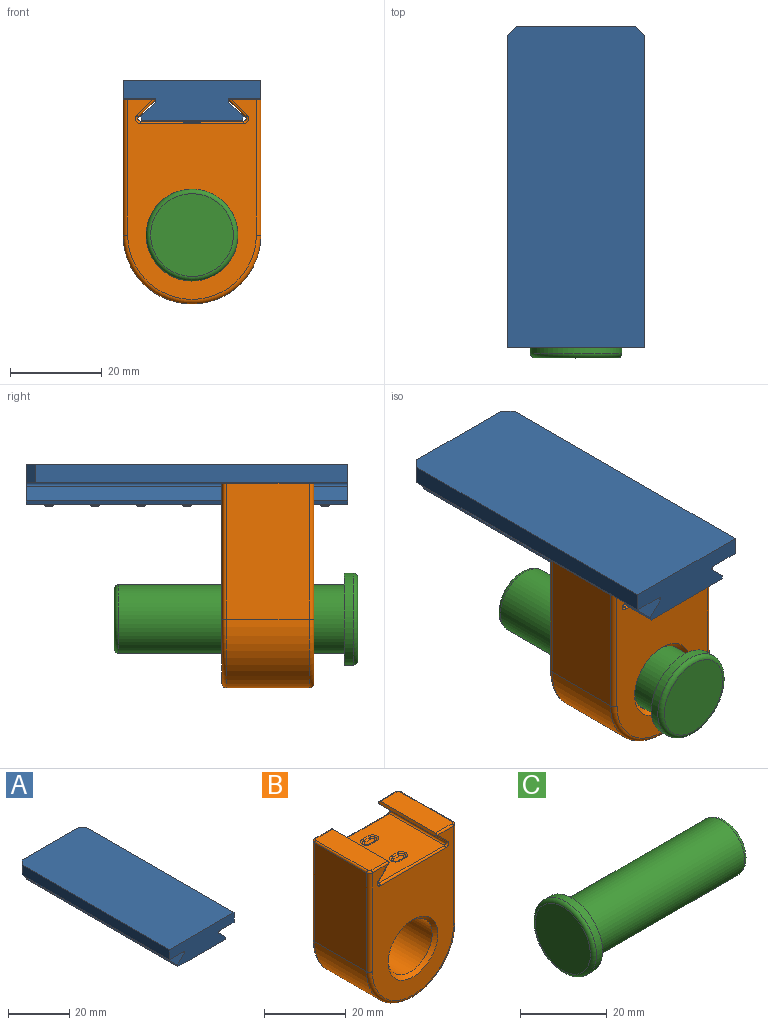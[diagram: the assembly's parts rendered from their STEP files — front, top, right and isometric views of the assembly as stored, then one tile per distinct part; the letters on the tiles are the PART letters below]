
ASSEMBLY  parts=3 mates=3
PART A: 79 faces, bbox 30x70x9.3 mm
  f0: cylinder r=0.5mm len=2mm, axis (-1,0,0), area 1mm2, adj f1,f2,f4,f59
  f1: torus R=1.37mm, axis (0,0,-1), area 1.9mm2, adj f0,f3,f5,f59
  f2: torus R=1.37mm, axis (0,0,-1), area 1.9mm2, adj f0,f3,f6,f59
  f3: cylinder r=0.5mm len=2mm, axis (1,0,0), area 1mm2, adj f1,f2,f7,f59
  f4: cylinder r=0.5mm len=2mm, axis (-1,0,0), area 1mm2, adj f0,f5,f6,f8
  f5: torus R=0.5mm, axis (0,0,-1), area 1.2mm2, adj f1,f4,f7,f8
  f6: torus R=0.5mm, axis (0,0,-1), area 1.2mm2, adj f2,f4,f7,f8
  f7: cylinder r=0.5mm len=2mm, axis (1,0,0), area 1mm2, adj f3,f5,f6,f8
  f8: plane 3x1mm, normal (0,0,-1), area 2.8mm2, adj f4,f5,f6,f7
  f9: cylinder r=0.5mm len=2mm, axis (-1,0,0), area 1mm2, adj f10,f11,f13,f59
  f10: torus R=1.37mm, axis (0,0,-1), area 1.9mm2, adj f9,f12,f14,f59
  f11: torus R=1.37mm, axis (0,0,-1), area 1.9mm2, adj f9,f12,f15,f59
  f12: cylinder r=0.5mm len=2mm, axis (1,0,0), area 1mm2, adj f10,f11,f16,f59
  f13: cylinder r=0.5mm len=2mm, axis (-1,0,0), area 1mm2, adj f9,f14,f15,f17
  f14: torus R=0.5mm, axis (0,0,-1), area 1.2mm2, adj f10,f13,f16,f17
  f15: torus R=0.5mm, axis (0,0,-1), area 1.2mm2, adj f11,f13,f16,f17
  f16: cylinder r=0.5mm len=2mm, axis (1,0,0), area 1mm2, adj f12,f14,f15,f17
  f17: plane 3x1mm, normal (0,0,-1), area 2.8mm2, adj f13,f14,f15,f16
  f18: cylinder r=0.5mm len=2mm, axis (-1,0,0), area 1mm2, adj f19,f20,f22,f59
  f19: torus R=1.37mm, axis (0,0,-1), area 1.9mm2, adj f18,f21,f23,f59
  f20: torus R=1.37mm, axis (0,0,-1), area 1.9mm2, adj f18,f21,f24,f59
  f21: cylinder r=0.5mm len=2mm, axis (1,0,0), area 1mm2, adj f19,f20,f25,f59
  f22: cylinder r=0.5mm len=2mm, axis (-1,0,0), area 1mm2, adj f18,f23,f24,f26
  f23: torus R=0.5mm, axis (0,0,-1), area 1.2mm2, adj f19,f22,f25,f26
  f24: torus R=0.5mm, axis (0,0,-1), area 1.2mm2, adj f20,f22,f25,f26
  f25: cylinder r=0.5mm len=2mm, axis (1,0,0), area 1mm2, adj f21,f23,f24,f26
  f26: plane 3x1mm, normal (0,0,-1), area 2.8mm2, adj f22,f23,f24,f25
  f27: cylinder r=0.5mm len=2mm, axis (-1,0,0), area 1mm2, adj f28,f29,f31,f59
  f28: torus R=1.37mm, axis (0,0,-1), area 1.9mm2, adj f27,f30,f32,f59
  f29: torus R=1.37mm, axis (0,0,-1), area 1.9mm2, adj f27,f30,f33,f59
  f30: cylinder r=0.5mm len=2mm, axis (1,0,0), area 1mm2, adj f28,f29,f34,f59
  f31: cylinder r=0.5mm len=2mm, axis (-1,0,0), area 1mm2, adj f27,f32,f33,f35
  f32: torus R=0.5mm, axis (0,0,-1), area 1.2mm2, adj f28,f31,f34,f35
  f33: torus R=0.5mm, axis (0,0,-1), area 1.2mm2, adj f29,f31,f34,f35
  f34: cylinder r=0.5mm len=2mm, axis (1,0,0), area 1mm2, adj f30,f32,f33,f35
  f35: plane 3x1mm, normal (0,0,-1), area 2.8mm2, adj f31,f32,f33,f34
  f36: cylinder r=0.5mm len=2mm, axis (-1,0,0), area 1mm2, adj f37,f38,f40,f59
  f37: torus R=1.37mm, axis (0,0,-1), area 1.9mm2, adj f36,f39,f41,f59
  f38: torus R=1.37mm, axis (0,0,-1), area 1.9mm2, adj f36,f39,f42,f59
  f39: cylinder r=0.5mm len=2mm, axis (1,0,0), area 1mm2, adj f37,f38,f43,f59
  f40: cylinder r=0.5mm len=2mm, axis (-1,0,0), area 1mm2, adj f36,f41,f42,f44
  f41: torus R=0.5mm, axis (0,0,-1), area 1.2mm2, adj f37,f40,f43,f44
  f42: torus R=0.5mm, axis (0,0,-1), area 1.2mm2, adj f38,f40,f43,f44
  f43: cylinder r=0.5mm len=2mm, axis (1,0,0), area 1mm2, adj f39,f41,f42,f44
  f44: plane 3x1mm, normal (0,0,-1), area 2.8mm2, adj f40,f41,f42,f43
  f45: cylinder r=0.5mm len=2mm, axis (-1,0,0), area 1mm2, adj f46,f47,f49,f59
  f46: torus R=1.37mm, axis (0,0,-1), area 1.9mm2, adj f45,f48,f50,f59
  f47: torus R=1.37mm, axis (0,0,-1), area 1.9mm2, adj f45,f48,f51,f59
  f48: cylinder r=0.5mm len=2mm, axis (1,0,0), area 1mm2, adj f46,f47,f52,f59
  f49: cylinder r=0.5mm len=2mm, axis (-1,0,0), area 1mm2, adj f45,f50,f51,f53
  f50: torus R=0.5mm, axis (0,0,-1), area 1.2mm2, adj f46,f49,f52,f53
  f51: torus R=0.5mm, axis (0,0,-1), area 1.2mm2, adj f47,f49,f52,f53
  f52: cylinder r=0.5mm len=2mm, axis (1,0,0), area 1mm2, adj f48,f50,f51,f53
  f53: plane 3x1mm, normal (0,0,-1), area 2.8mm2, adj f49,f50,f51,f52
  f54: plane 68x4mm, normal (1,0,0), area 272mm2, adj f55,f61,f62,f69
  f55: plane 70x30mm, normal (0,0,1), area 2096mm2, adj f54,f56,f62,f63,f68,f69
  f56: plane 68x4mm, normal (-1,0,0), area 272mm2, adj f55,f57,f62,f68
  f57: plane 70x6.65mm, normal (0,0,-1), area 463.3mm2, adj f56,f62,f63,f66,f68
  f58: plane 70x3.19mm, normal (-0.71,0,0.71), area 315.7mm2, adj f62,f63,f65,f66
  f59: plane 70x21.79mm, normal (0,0,-1), area 1446.2mm2, adj f0,f1,f2,f3,f9,f10,f11,f12
  f60: plane 70x3.19mm, normal (0.71,0,0.71), area 315.7mm2, adj f62,f63,f64,f67
  f61: plane 70x6.65mm, normal (0,0,-1), area 463.3mm2, adj f54,f62,f63,f67,f69
  f62: plane 30x8.75mm, normal (0,-1,0), area 210.4mm2, adj f54,f55,f56,f57,f58,f59,f60,f61
  f63: plane 26x8.75mm, normal (0,1,0), area 194.4mm2, adj f55,f57,f58,f59,f60,f61,f64,f65
  f64: plane 70x0.71mm, normal (0.92,0,-0.38), area 53.6mm2, adj f59,f60,f62,f63
  f65: plane 70x0.71mm, normal (-0.92,0,-0.38), area 53.6mm2, adj f58,f59,f62,f63
  f66: cylinder r=0.5mm len=70mm, axis (0,-1,0), area 82.5mm2, adj f57,f58,f62,f63
  f67: cylinder r=0.5mm len=70mm, axis (0,-1,0), area 82.5mm2, adj f60,f61,f62,f63
  f68: plane 4x2mm, normal (-0.71,0.71,0), area 11.3mm2, adj f55,f56,f57,f63
  f69: plane 4x2mm, normal (0.71,0.71,0), area 11.3mm2, adj f54,f55,f61,f63
  f70: plane 3x1mm, normal (0,0,-1), area 2.8mm2, adj f71,f72,f73,f74
  f71: cylinder r=0.5mm len=2mm, axis (-1,0,0), area 1mm2, adj f70,f72,f73,f75
  f72: torus R=0.5mm, axis (0,0,-1), area 1.2mm2, adj f70,f71,f74,f76
  f73: torus R=0.5mm, axis (0,0,-1), area 1.2mm2, adj f70,f71,f74,f77
  f74: cylinder r=0.5mm len=2mm, axis (1,0,0), area 1mm2, adj f70,f72,f73,f78
  f75: cylinder r=0.5mm len=2mm, axis (-1,0,0), area 1mm2, adj f59,f71,f76,f77
  f76: torus R=1.37mm, axis (0,0,-1), area 1.9mm2, adj f59,f72,f75,f78
  f77: torus R=1.37mm, axis (0,0,-1), area 1.9mm2, adj f59,f73,f75,f78
  f78: cylinder r=0.5mm len=2mm, axis (1,0,0), area 1mm2, adj f59,f74,f76,f77
PART B: 61 faces, bbox 32.5x20.2x46.2 mm
  f0: cylinder r=0.5mm len=2mm, axis (1,0,0), area 1mm2, adj f1,f2,f4,f8
  f1: torus R=0.63mm, axis (0,0,-1), area 1.4mm2, adj f0,f3,f5,f8
  f2: torus R=0.63mm, axis (0,0,-1), area 1.4mm2, adj f0,f3,f6,f8
  f3: cylinder r=0.5mm len=2mm, axis (-1,0,0), area 1mm2, adj f1,f2,f7,f8
  f4: cylinder r=0.5mm len=2mm, axis (1,0,0), area 1mm2, adj f0,f5,f6,f9
  f5: torus R=1.5mm, axis (0,0,1), area 2.1mm2, adj f1,f4,f7,f9
  f6: torus R=1.5mm, axis (0,0,1), area 2.1mm2, adj f2,f4,f7,f9
  f7: cylinder r=0.5mm len=2mm, axis (-1,0,0), area 1mm2, adj f3,f5,f6,f9
  f8: plane 3.27x1.27mm, normal (0,0,1), area 3.8mm2, adj f0,f1,f2,f3
  f9: plane 22.59x19mm, normal (0,0,1), area 403mm2, adj f4,f5,f6,f7,f22,f23,f25,f26
  f10: plane 29.5x18mm, normal (-1,0,0), area 531mm2, adj f11,f37,f40,f43
  f11: cylinder r=15mm len=30mm, axis (0,1,0), area 848.2mm2, adj f10,f12,f36,f39
  f12: plane 29.5x18mm, normal (1,0,0), area 531mm2, adj f11,f35,f38,f48
  f13: plane 19x6.2mm, normal (0,0,1), area 117.7mm2, adj f20,f46,f47,f48,f49,f50
  f14: plane 19x3.64mm, normal (-0.71,0,-0.71), area 97.8mm2, adj f20,f22,f51,f56
  f15: plane 19x3.64mm, normal (0.71,0,-0.71), area 97.8mm2, adj f21,f23,f55,f60
  f16: cylinder r=7.6mm len=18mm, axis (0,1,0), area 859.5mm2, adj f33,f34
  f17: plane 19x6.2mm, normal (0,0,1), area 117.7mm2, adj f21,f41,f42,f43,f44,f45
  f18: plane 43.5x28mm, normal (0,-1,0), area 788.5mm2, adj f34,f38,f39,f40,f41,f46,f51,f52
  f19: plane 43.5x28mm, normal (0,1,0), area 788.5mm2, adj f33,f35,f36,f37,f45,f50,f56,f57
  f20: plane 19.96x0.71mm, normal (-0.92,0,0.38), area 15.1mm2, adj f13,f14,f46,f50,f51,f56
  f21: plane 19.96x0.71mm, normal (0.92,0,0.38), area 15.1mm2, adj f15,f17,f41,f45,f55,f60
  f22: cylinder r=0.5mm len=19mm, axis (0,-1,0), area 22.4mm2, adj f9,f14,f52,f57
  f23: cylinder r=0.5mm len=19mm, axis (0,-1,0), area 22.4mm2, adj f9,f15,f54,f59
  f24: plane 3.27x1.27mm, normal (0,0,1), area 3.8mm2, adj f29,f30,f31,f32
  f25: cylinder r=0.5mm len=2mm, axis (1,0,0), area 1mm2, adj f9,f26,f27,f29
  f26: torus R=1.5mm, axis (0,0,1), area 2.1mm2, adj f9,f25,f28,f30
  f27: torus R=1.5mm, axis (0,0,1), area 2.1mm2, adj f9,f25,f28,f31
  f28: cylinder r=0.5mm len=2mm, axis (-1,0,0), area 1mm2, adj f9,f26,f27,f32
  f29: cylinder r=0.5mm len=2mm, axis (1,0,0), area 1mm2, adj f24,f25,f30,f31
  f30: torus R=0.63mm, axis (0,0,-1), area 1.4mm2, adj f24,f26,f29,f32
  f31: torus R=0.63mm, axis (0,0,-1), area 1.4mm2, adj f24,f27,f29,f32
  f32: cylinder r=0.5mm len=2mm, axis (-1,0,0), area 1mm2, adj f24,f28,f30,f31
  f33: cone r=8.6mm half-angle=45deg, axis (0,1,0), area 72mm2, adj f16,f19
  f34: cone r=7.6mm half-angle=45deg, axis (0,-1,0), area 72mm2, adj f16,f18
  f35: cylinder r=1mm len=29.5mm, axis (0,0,1), area 46.3mm2, adj f12,f19,f36,f49
  f36: torus R=14mm, axis (0,-1,0), area 72.2mm2, adj f11,f19,f35,f37
  f37: cylinder r=1mm len=29.5mm, axis (0,0,-1), area 46.3mm2, adj f10,f19,f36,f44
  f38: cylinder r=1mm len=29.5mm, axis (0,0,-1), area 46.3mm2, adj f12,f18,f39,f47
  f39: torus R=14mm, axis (0,-1,0), area 72.2mm2, adj f11,f18,f38,f40
  f40: cylinder r=1mm len=29.5mm, axis (0,0,1), area 46.3mm2, adj f10,f18,f39,f42
  f41: cylinder r=0.5mm len=5.85mm, axis (1,0,0), area 4.5mm2, adj f17,f18,f21,f42,f55
  f42: torus R=0.5mm, axis (0,0,1), area 1mm2, adj f17,f40,f41,f43
  f43: cylinder r=0.5mm len=18mm, axis (0,1,0), area 14.1mm2, adj f10,f17,f42,f44
  f44: torus R=0.5mm, axis (0,0,1), area 1mm2, adj f17,f37,f43,f45
  f45: cylinder r=0.5mm len=5.85mm, axis (-1,0,0), area 4.5mm2, adj f17,f19,f21,f44,f60
  f46: cylinder r=0.5mm len=5.85mm, axis (1,0,0), area 4.5mm2, adj f13,f18,f20,f47,f51
  f47: torus R=0.5mm, axis (0,0,1), area 1mm2, adj f13,f38,f46,f48
  f48: cylinder r=0.5mm len=18mm, axis (0,1,0), area 14.1mm2, adj f12,f13,f47,f49
  f49: torus R=0.5mm, axis (0,0,1), area 1mm2, adj f13,f35,f48,f50
  f50: cylinder r=0.5mm len=5.85mm, axis (-1,0,0), area 4.5mm2, adj f13,f19,f20,f49,f56
  f51: cylinder r=0.5mm len=4.1mm, axis (-0.71,0,0.71), area 4.1mm2, adj f14,f18,f20,f46,f52
  f52: torus R=1mm, axis (0,-1,0), area 1.3mm2, adj f18,f22,f51,f53
  f53: cylinder r=0.5mm len=22.59mm, axis (1,0,0), area 17.7mm2, adj f9,f18,f52,f54
  f54: torus R=1mm, axis (0,-1,0), area 1.3mm2, adj f18,f23,f53,f55
  f55: cylinder r=0.5mm len=4.1mm, axis (-0.71,0,-0.71), area 4.1mm2, adj f15,f18,f21,f41,f54
  f56: cylinder r=0.5mm len=4.1mm, axis (0.71,0,-0.71), area 4.1mm2, adj f14,f19,f20,f50,f57
  f57: torus R=1mm, axis (0,-1,0), area 1.3mm2, adj f19,f22,f56,f58
  f58: cylinder r=0.5mm len=22.59mm, axis (-1,0,0), area 17.7mm2, adj f9,f19,f57,f59
  f59: torus R=1mm, axis (0,-1,0), area 1.3mm2, adj f19,f23,f58,f60
  f60: cylinder r=0.5mm len=4.1mm, axis (0.71,0,0.71), area 4.1mm2, adj f15,f19,f21,f45,f59
PART C: 7 faces, bbox 53x21.6x21.6 mm
  f0: cylinder r=7.45mm len=49mm, axis (-1,0,0), area 2293.7mm2, adj f2,f5
  f1: plane 12.9x12.9mm, normal (1,0,0), area 130.7mm2, adj f2
  f2: torus R=6.45mm, axis (1,0,0), area 69.9mm2, adj f0,f1
  f3: cylinder r=10mm len=20mm, axis (1,0,0), area 125.7mm2, adj f5,f6
  f4: plane 18x18mm, normal (-1,0,0), area 254.5mm2, adj f6
  f5: plane 20x20mm, normal (1,0,0), area 139.8mm2, adj f0,f3
  f6: torus R=9mm, axis (-1,0,0), area 95.1mm2, adj f3,f4
PLACE A t=(-23.82,10.52,-11.33)mm fixed
PLACE B t=(-23.82,-42.1,-45.08)mm
PLACE C rot(axis=(-0.44,-0.44,0.78),104deg) t=(-23.82,-58.67,-45.08)mm
MATE slider A.f62 <-> B.f18  axis (0,-1,0) through (-23.82,-59.48,-15.28)mm
MATE parallel C.f3 <-> B.f18  axis (0,1,0) through (-23.82,-58.67,-45.08)mm
MATE cylindrical B.f16 <-> C.f0  axis (0,1,0) through (-23.82,-51.1,-45.08)mm
